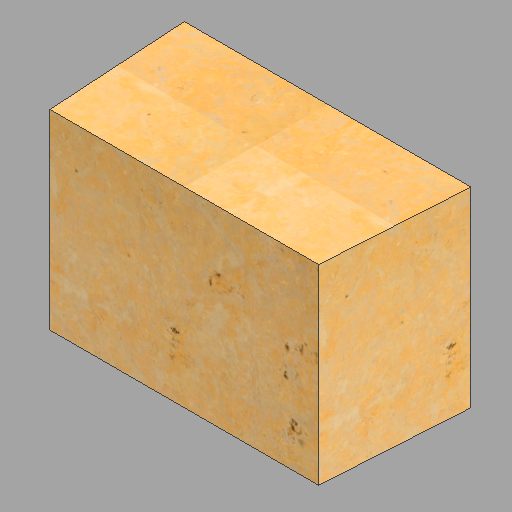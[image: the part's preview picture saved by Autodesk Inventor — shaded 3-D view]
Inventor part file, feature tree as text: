
AUTODESK INVENTOR PART (.ipt)
format: ipt  version: 2023 (Build 270158030, 158C)  size: 398,336 bytes
history: native  units: in
note: dims shown in document units (in); Inventor stores cm internally (conversion verified against a paired STEP export)
features: extrude x1, sketch x1
ambient origin geometry x8: Origin, YZ Plane, XZ Plane, XY Plane, X Axis, Y Axis, Z Axis, Center Point
bodies: Solid1 (feature_tree)
feature tree (2):
  extrude  "Extrusion1"  Depth=18.0in
  sketch  "Sketch1"  dims[d0=36.0in d2=18.0in d3=0.0493in d4=24.0in d5=0.0in]
